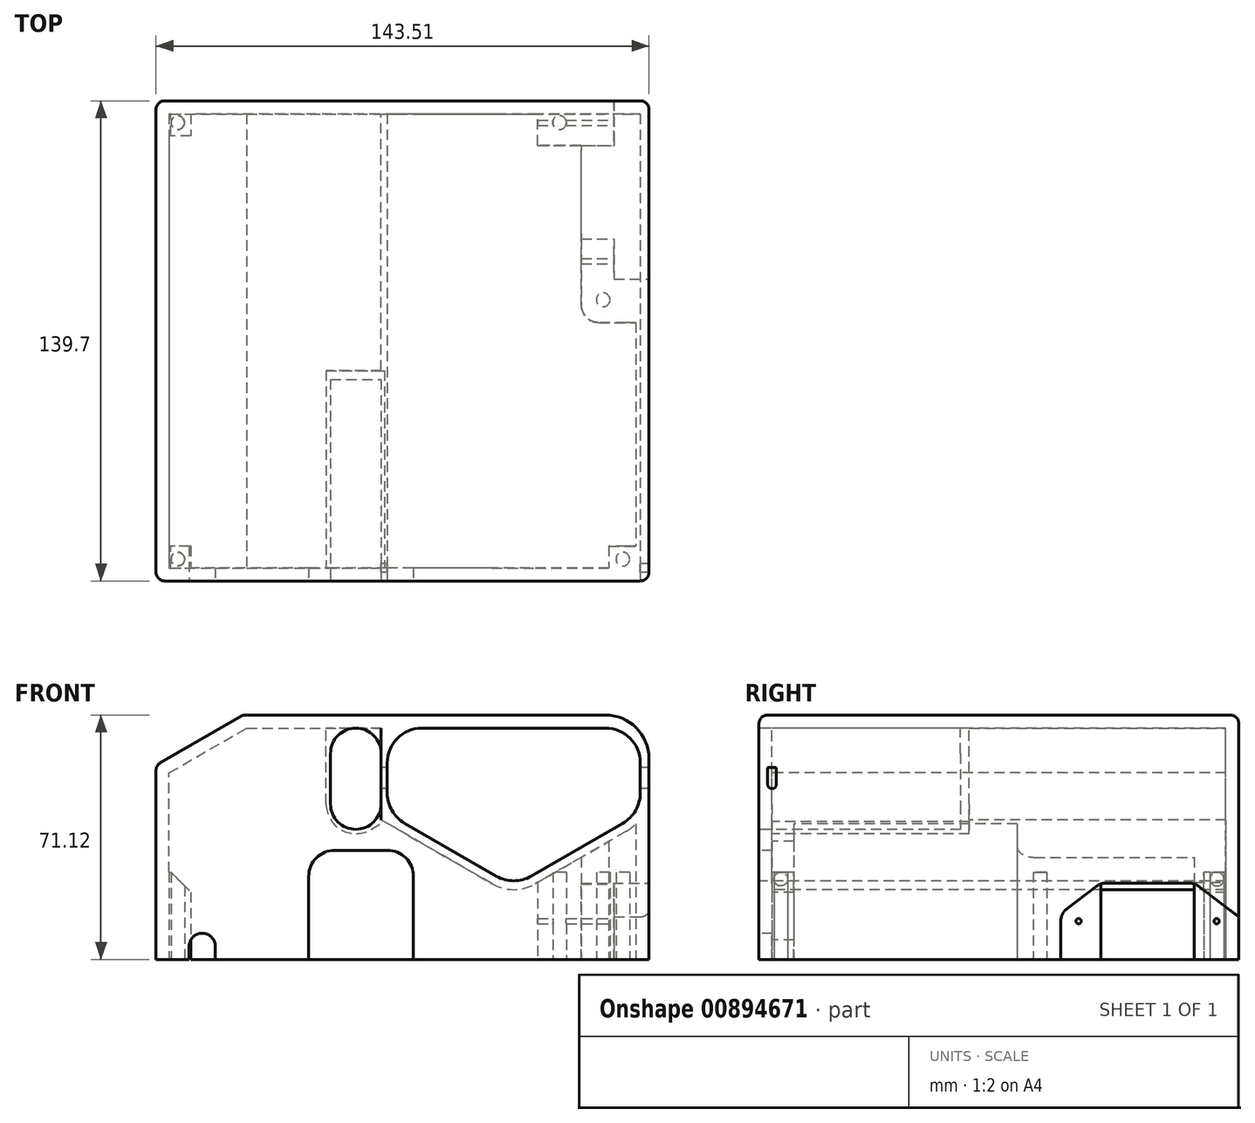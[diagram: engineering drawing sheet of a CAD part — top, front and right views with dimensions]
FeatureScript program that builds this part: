
annotation { "Feature Type Name" : "Feature", "Feature Type Description" : "" }
export const myFeature = defineFeature(function(context is Context, id is Id, definition is map)
    precondition{}
    {
        {
            var Q0;
            Q0=qCreatedBy(makeId("Top.planeOp"),FACE);
            var sketch = newSketch(context, id + "F0", { "sketchPlane" : qUnion([Q0])});
            skCircle(sketch, "E0", {"center": v(0, 127) * mm, "radius": 2 * mm});
            skCircle(sketch, "E1", {"center": v(0, 0) * mm, "radius": 2 * mm});
            skCircle(sketch, "E2", {"center": v(129.54, 0) * mm, "radius": 2 * mm});
            skCircle(sketch, "E3", {"center": v(123.83, 75.44) * mm, "radius": 2 * mm});
            skCircle(sketch, "E4", {"center": v(111.13, 127) * mm, "radius": 2 * mm});
            skSolve(sketch);
        }
        {
            var Q0;
            Q0=qCreatedBy(makeId("Front.planeOp"),FACE);
            var sketch = newSketch(context, id + "F1", { "sketchPlane" : qUnion([Q0])});
            skLineSegment(sketch, "E5", {"start": v(-6.35, 0) * mm, "end": v(-6.35, 56.46) * mm});
            skLineSegment(sketch, "E6", {"start": v(-6.35, 56.46) * mm, "end": v(19.05, 71.12) * mm});
            skLineSegment(sketch, "E7", {"start": v(19.05, 71.12) * mm, "end": v(124.46, 71.12) * mm});
            skLineSegment(sketch, "E8", {"start": v(137.16, 58.42) * mm, "end": v(137.16, 0) * mm});
            skLineSegment(sketch, "E9", {"start": v(137.16, 0) * mm, "end": v(-6.35, 0) * mm});
            skArc(sketch, "E10.filletArc", {"start": v(137.16, 58.42) * mm, "mid": v(133.44, 67.4) * mm, "end": v(124.46, 71.12) * mm});
            skSolve(sketch);
        }
        {
            var Q0;
            Q0=makeQuery(id+"F1.imprint","IMPRINT",FACE,{"disambiguationData":[TD([[makeQuery(id+"F1.imprint","IMPRINT",EDGE,{"derivedFrom":sQuery(id+"F1.wireOp",EDGE,"E5")}),-1.0]])]});
            extrude(context, id + "F2", {"entities" : qUnion([Q0]), "oppositeDirection" : true, "depth" : 133.35 * mm, "offsetDistance" : 25.4 * mm, "hasSecondDirection" : true, "secondDirectionOppositeDirection" : false, "secondDirectionDepth" : 6.35 * mm});
        }
        {
            var Q0;
            Q0=makeQuery(id+"F2.opExtrude","SWEPT_FACE",FACE,{"disambiguationData":[OSD([sQuery(id+"F1.wireOp",EDGE,"E9")])]});
            shell(context, id + "F3", {"entities" : qUnion([Q0]), "thickness" : 3.8 * mm});
        }
        {
            var Q0;
            Q0=makeQuery(id+"F2.opExtrude","SWEPT_FACE",FACE,{"disambiguationData":[OSD([sQuery(id+"F1.wireOp",EDGE,"E9")])]});
            var sketch = newSketch(context, id + "F4", { "sketchPlane" : qUnion([Q0])});
            skLineSegment(sketch, "E11", {"start": v(104.78, -129.54) * mm, "end": v(104.78, -120.4) * mm});
            skLineSegment(sketch, "E12", {"start": v(104.78, -120.4) * mm, "end": v(117.48, -120.4) * mm});
            skLineSegment(sketch, "E13", {"start": v(117.48, -120.4) * mm, "end": v(117.48, -68.83) * mm});
            skLineSegment(sketch, "E14", {"start": v(117.48, -68.83) * mm, "end": v(133.35, -68.83) * mm});
            skLineSegment(sketch, "E15", {"start": v(133.35, -68.83) * mm, "end": v(133.35, -129.54) * mm});
            skLineSegment(sketch, "E16", {"start": v(133.35, -129.54) * mm, "end": v(104.78, -129.54) * mm});
            skSolve(sketch);
        }
        {
            var Q0;
            Q0=makeQuery(id+"F4.imprint","IMPRINT",FACE,{"disambiguationData":[TD([[makeQuery(id+"F4.imprint","IMPRINT",EDGE,{"derivedFrom":sQuery(id+"F4.wireOp",EDGE,"E11")}),-1.0]])]});
            extrude(context, id + "F5", {"entities" : qUnion([Q0]), "operationType" : NewBodyOperationType.ADD, "endBound" : BoundingType.UP_TO_NEXT, "oppositeDirection" : true, "depth" : 25.4 * mm, "offsetDistance" : 25.4 * mm});
        }
        {
            var Q0;
            Q0=makeQuery(id+"F2.opExtrude","SWEPT_FACE",FACE,{"disambiguationData":[OSD([sQuery(id+"F1.wireOp",EDGE,"E8")])]});
            var sketch = newSketch(context, id + "F6", { "sketchPlane" : qUnion([Q0])});
            skArc(sketch, "E17", {"start": v(83.35, 14.77) * mm, "mid": v(82.01, 13.16) * mm, "end": v(81.53, 11.13) * mm});
            skLineSegment(sketch, "E18", {"start": v(83.35, 14.77) * mm, "end": v(91.97, 21.3) * mm});
            skLineSegment(sketch, "E19", {"start": v(94.73, 22.22) * mm, "end": v(118.86, 22.22) * mm});
            skLineSegment(sketch, "E20", {"start": v(121.62, 21.3) * mm, "end": v(133.35, 12.41) * mm});
            skLineSegment(sketch, "E21", {"start": v(133.35, 12.41) * mm, "end": v(133.35, 0) * mm});
            skPoint(sketch, "E22.visualSharp", {"position": v(93.19, 22.22) * mm});
            skArc(sketch, "E22.filletArc", {"start": v(94.73, 22.22) * mm, "mid": v(93.27, 21.99) * mm, "end": v(91.97, 21.3) * mm});
            skPoint(sketch, "E23.visualSharp", {"position": v(120.4, 22.23) * mm});
            skArc(sketch, "E23.filletArc", {"start": v(121.62, 21.3) * mm, "mid": v(120.31, 21.99) * mm, "end": v(118.86, 22.22) * mm});
            skLineSegment(sketch, "E24", {"start": v(81.53, -2.54) * mm, "end": v(133.35, -2.54) * mm});
            skLineSegment(sketch, "E25", {"start": v(133.35, -2.54) * mm, "end": v(133.35, 0) * mm});
            skLineSegment(sketch, "E26", {"start": v(81.53, 11.13) * mm, "end": v(81.53, -2.54) * mm});
            skSolve(sketch);
        }
        {
            var Q0;
            {var subQ4=sQuery(id+"F6.wireOp",EDGE,"E17");Q0=makeQuery(id+"F6.imprint","IMPRINT",FACE,{"disambiguationData":[TD([[makeQuery(id+"F6.imprint","IMPRINT",EDGE,{"derivedFrom":subQ4}),1.0]])]});}
            extrude(context, id + "F7", {"entities" : qUnion([Q0]), "operationType" : NewBodyOperationType.REMOVE, "oppositeDirection" : true, "depth" : 10.16 * mm, "offsetDistance" : 25.4 * mm});
        }
        {
            var Q0;
            Q0=makeQuery(id+"F7.boolean.opBoolean","COPY",FACE,{"derivedFrom":makeQuery(id+"F7.opExtrude","CAP_FACE",FACE,{"disambiguationData":[OSD([sQuery(id+"F1.wireOp",EDGE,"E8"),sQuery(id+"F1.wireOp",EDGE,"E9"),sQuery(id+"F6.wireOp",EDGE,"kEtzdfqh-l9jc-MdX5-V50T-5vboHq0TSI4w"),sQuery(id+"F6.wireOp",EDGE,"E17"),sQuery(id+"F6.wireOp",EDGE,"E18"),sQuery(id+"F6.wireOp",EDGE,"E19"),sQuery(id+"F6.wireOp",EDGE,"E20"),sQuery(id+"F6.wireOp",EDGE,"E21"),sQuery(id+"F6.wireOp",EDGE,"E22.filletArc"),sQuery(id+"F6.wireOp",EDGE,"E23.filletArc"),sQuery(id+"F6.wireOp",EDGE,"10d31ba4-3e29-4994-a5b2-82bfb8ec1515.filletArc")])],"isStart":false})});
            var sketch = newSketch(context, id + "F8", { "sketchPlane" : qUnion([Q0])});
            skLineSegment(sketch, "E27", {"start": v(93.22, 22.23) * mm, "end": v(120.4, 22.23) * mm});
            skLineSegment(sketch, "E28", {"start": v(120.4, 22.23) * mm, "end": v(120.4, 0) * mm});
            skLineSegment(sketch, "E29", {"start": v(120.4, 0) * mm, "end": v(93.22, 0) * mm});
            skLineSegment(sketch, "E30", {"start": v(93.22, 0) * mm, "end": v(93.22, 22.23) * mm});
            skCircle(sketch, "E31", {"center": v(86.72, 11.13) * mm, "radius": 0.76 * mm});
            skCircle(sketch, "E32", {"center": v(126.9, 11.13) * mm, "radius": 0.76 * mm});
            skSolve(sketch);
        }
        {
            var Q0;
            {var subQ0=sQuery(id+"F8.wireOp",EDGE,"E27");var subQ1=makeQuery(id+"F7.boolean.opBoolean","COPY",EDGE,{"derivedFrom":makeQuery(id+"F7.opExtrude","CAP_EDGE",EDGE,{"disambiguationData":[OSD([sQuery(id+"F6.wireOp",EDGE,"E22.filletArc")])],"isStart":false})});var subQ2=makeQuery(id+"F8.imprint","INTERSECT",VERTEX,{"derivedFrom":[subQ1,subQ0]});Q0=makeQuery(id+"F8.imprint","IMPRINT",FACE,{"disambiguationData":[TD([[makeQuery(id+"F8.imprint","IMPRINT",EDGE,{"disambiguationData":[TD([[subQ2,-1.0]])],"derivedFrom":subQ0}),-1.0]])]});}
            var Q1;
            Q1=makeQuery(id+"F8.imprint","IMPRINT",FACE,{"disambiguationData":[TD([[makeQuery(id+"F8.imprint","IMPRINT",EDGE,{"derivedFrom":sQuery(id+"F8.wireOp",EDGE,"E32")}),1.0]])]});
            var Q2;
            Q2=makeQuery(id+"F8.imprint","IMPRINT",FACE,{"disambiguationData":[TD([[makeQuery(id+"F8.imprint","IMPRINT",EDGE,{"derivedFrom":sQuery(id+"F8.wireOp",EDGE,"E31")}),1.0]])]});
            extrude(context, id + "F9", {"entities" : qUnion([Q0, Q1, Q2]), "operationType" : NewBodyOperationType.REMOVE, "oppositeDirection" : true, "depth" : 25.4 * mm, "offsetDistance" : 25.4 * mm});
        }
        {
            var Q0;
            Q0=makeQuery(id+"F2.opExtrude","CAP_FACE",FACE,{"disambiguationData":[OSD([sQuery(id+"F1.wireOp",EDGE,"E5"),sQuery(id+"F1.wireOp",EDGE,"E6"),sQuery(id+"F1.wireOp",EDGE,"E7"),sQuery(id+"F1.wireOp",EDGE,"E8"),sQuery(id+"F1.wireOp",EDGE,"E9"),sQuery(id+"F1.wireOp",EDGE,"E10.filletArc")])],"isStart":true});
            var sketch = newSketch(context, id + "F10", { "sketchPlane" : qUnion([Q0])});
            skArc(sketch, "E33", {"start": v(134.62, 57.15) * mm, "mid": v(131.64, 64.33) * mm, "end": v(124.46, 67.31) * mm});
            skArc(sketch, "E34", {"start": v(71.12, 67.31) * mm, "mid": v(63.94, 64.33) * mm, "end": v(60.96, 57.15) * mm});
            skLineSegment(sketch, "E35", {"start": v(71.12, 67.31) * mm, "end": v(124.46, 67.31) * mm});
            skLineSegment(sketch, "E36", {"start": v(134.62, 57.15) * mm, "end": v(134.62, 48.42) * mm});
            skLineSegment(sketch, "E37", {"start": v(60.96, 57.15) * mm, "end": v(60.96, 48.42) * mm});
            skArc(sketch, "E38", {"start": v(60.96, 48.42) * mm, "mid": v(62.32, 43.34) * mm, "end": v(66.04, 39.62) * mm});
            skArc(sketch, "E39", {"start": v(129.54, 39.62) * mm, "mid": v(133.26, 43.34) * mm, "end": v(134.62, 48.42) * mm});
            skLineSegment(sketch, "E40", {"start": v(66.04, 39.62) * mm, "end": v(92.71, 24.22) * mm});
            skLineSegment(sketch, "E41", {"start": v(102.87, 24.22) * mm, "end": v(129.54, 39.62) * mm});
            skArc(sketch, "E42", {"start": v(92.71, 24.22) * mm, "mid": v(97.8, 22.86) * mm, "end": v(102.87, 24.22) * mm});
            skArc(sketch, "E43", {"start": v(59.18, 59.94) * mm, "mid": v(51.82, 67.31) * mm, "end": v(44.45, 59.94) * mm});
            skArc(sketch, "E44", {"start": v(44.45, 45.21) * mm, "mid": v(51.82, 37.85) * mm, "end": v(59.18, 45.21) * mm});
            skLineSegment(sketch, "E45", {"start": v(44.45, 59.94) * mm, "end": v(44.45, 45.21) * mm});
            skLineSegment(sketch, "E46", {"start": v(59.18, 59.94) * mm, "end": v(59.18, 45.21) * mm});
            skLineSegment(sketch, "E47", {"start": v(56.93, 37.85) * mm, "end": v(38.82, 37.85) * mm, "construction": true});
            skSolve(sketch);
        }
        {
            var Q0;
            Q0 = qSketchRegion(id + "F10", true);
            var Q1;
            {var subQ0=sQuery(id+"F1.wireOp",EDGE,"E10.filletArc");var subQ1=sQuery(id+"F1.wireOp",EDGE,"E9");var subQ2=sQuery(id+"F1.wireOp",EDGE,"E8");var subQ3=sQuery(id+"F1.wireOp",EDGE,"E7");var subQ4=sQuery(id+"F1.wireOp",EDGE,"E6");var subQ5=sQuery(id+"F1.wireOp",EDGE,"E5");Q1=makeQuery(id+"F3.opShell","OFFSET_FACE",FACE,{"disambiguationData":[OSD([subQ5,subQ4,subQ3,subQ2,subQ1,subQ0]),TDD([makeQuery(id+"F2.opExtrude","CAP_FACE",FACE,{"disambiguationData":[OSD([subQ5,subQ4,subQ3,subQ2,subQ1,subQ0])],"isStart":false})])]});}
            extrude(context, id + "F11", {"entities" : qUnion([Q0]), "operationType" : NewBodyOperationType.REMOVE, "endBound" : BoundingType.UP_TO_SURFACE, "oppositeDirection" : true, "depth" : 25.4 * mm, "endBoundEntityFace" : qUnion([Q1]), "offsetDistance" : 25.4 * mm});
        }
        {
            var Q0;
            Q0=makeQuery(id+"F2.opExtrude","CAP_FACE",FACE,{"disambiguationData":[OSD([sQuery(id+"F1.wireOp",EDGE,"E5"),sQuery(id+"F1.wireOp",EDGE,"E6"),sQuery(id+"F1.wireOp",EDGE,"E7"),sQuery(id+"F1.wireOp",EDGE,"E8"),sQuery(id+"F1.wireOp",EDGE,"E9"),sQuery(id+"F1.wireOp",EDGE,"E10.filletArc")])],"isStart":true});
            var sketch = newSketch(context, id + "F12", { "sketchPlane" : qUnion([Q0])});
            skArc(sketch, "E48", {"start": v(91.44, 22.02) * mm, "mid": v(97.8, 20.32) * mm, "end": v(104.14, 22.02) * mm});
            skLineSegment(sketch, "E49", {"start": v(91.44, 22.02) * mm, "end": v(59.18, 40.65) * mm});
            skLineSegment(sketch, "E50", {"start": v(104.14, 22.02) * mm, "end": v(130.48, 37.23) * mm});
            skLineSegment(sketch, "E51", {"start": v(59.18, 71.12) * mm, "end": v(124.46, 71.12) * mm});
            skArc(sketch, "E52", {"start": v(137.16, 58.42) * mm, "mid": v(133.44, 67.4) * mm, "end": v(124.46, 71.12) * mm});
            skLineSegment(sketch, "E53", {"start": v(137.16, 58.42) * mm, "end": v(137.16, 48.8) * mm});
            skArc(sketch, "E54", {"start": v(130.48, 37.23) * mm, "mid": v(135.37, 42.12) * mm, "end": v(137.16, 48.8) * mm});
            skLineSegment(sketch, "E55", {"start": v(92.71, 24.22) * mm, "end": v(66.04, 39.62) * mm});
            skLineSegment(sketch, "E56", {"start": v(71.12, 67.31) * mm, "end": v(124.46, 67.31) * mm});
            skLineSegment(sketch, "E57", {"start": v(134.62, 57.15) * mm, "end": v(134.62, 48.42) * mm});
            skLineSegment(sketch, "E58", {"start": v(129.54, 39.62) * mm, "end": v(102.87, 24.22) * mm});
            skArc(sketch, "E59", {"start": v(92.71, 24.22) * mm, "mid": v(97.8, 22.86) * mm, "end": v(102.87, 24.22) * mm});
            skArc(sketch, "E60", {"start": v(129.54, 39.62) * mm, "mid": v(133.26, 43.34) * mm, "end": v(134.62, 48.42) * mm});
            skArc(sketch, "E61", {"start": v(134.62, 57.15) * mm, "mid": v(131.64, 64.33) * mm, "end": v(124.46, 67.31) * mm});
            skArc(sketch, "E62", {"start": v(71.12, 67.31) * mm, "mid": v(63.94, 64.33) * mm, "end": v(60.96, 57.15) * mm});
            skLineSegment(sketch, "E63", {"start": v(60.96, 57.15) * mm, "end": v(60.96, 48.42) * mm});
            skArc(sketch, "E64", {"start": v(60.96, 48.42) * mm, "mid": v(62.32, 43.34) * mm, "end": v(66.04, 39.62) * mm});
            skLineSegment(sketch, "E65", {"start": v(59.18, 71.12) * mm, "end": v(59.18, 40.65) * mm});
            skSolve(sketch);
        }
        {
            var Q0;
            Q0=makeQuery(id+"F12.imprint","IMPRINT",FACE,{"disambiguationData":[TD([[makeQuery(id+"F12.imprint","IMPRINT",EDGE,{"derivedFrom":sQuery(id+"F12.wireOp",EDGE,"E48")}),1.0]])]});
            var Q1;
            {var subQ0=sQuery(id+"F1.wireOp",EDGE,"E10.filletArc");var subQ1=sQuery(id+"F1.wireOp",EDGE,"E9");var subQ2=sQuery(id+"F1.wireOp",EDGE,"E8");var subQ3=sQuery(id+"F1.wireOp",EDGE,"E7");var subQ4=sQuery(id+"F1.wireOp",EDGE,"E6");var subQ5=sQuery(id+"F1.wireOp",EDGE,"E5");Q1=makeQuery(id+"F11.boolean.opBoolean","MERGE",FACE,{"derivedFrom":[makeQuery(id+"F3.opShell","OFFSET_FACE",FACE,{"disambiguationData":[OSD([subQ5,subQ4,subQ3,subQ2,subQ1,subQ0]),TDD([makeQuery(id+"F2.opExtrude","CAP_FACE",FACE,{"disambiguationData":[OSD([subQ5,subQ4,subQ3,subQ2,subQ1,subQ0])],"isStart":false})])]})],"fromTools":[makeQuery(id+"F11.opExtrude","CAP_FACE",FACE,{"disambiguationData":[OSD([sQuery(id+"F10.wireOp",EDGE,"E33"),sQuery(id+"F10.wireOp",EDGE,"E34"),sQuery(id+"F10.wireOp",EDGE,"E35"),sQuery(id+"F10.wireOp",EDGE,"E36"),sQuery(id+"F10.wireOp",EDGE,"E37"),sQuery(id+"F10.wireOp",EDGE,"E38"),sQuery(id+"F10.wireOp",EDGE,"E39"),sQuery(id+"F10.wireOp",EDGE,"E40"),sQuery(id+"F10.wireOp",EDGE,"E41"),sQuery(id+"F10.wireOp",EDGE,"E42")])],"isStart":false})]});}
            extrude(context, id + "F13", {"entities" : qUnion([Q0]), "operationType" : NewBodyOperationType.ADD, "endBound" : BoundingType.UP_TO_SURFACE, "oppositeDirection" : true, "depth" : 25.4 * mm, "endBoundEntityFace" : qUnion([Q1]), "offsetDistance" : 25.4 * mm});
        }
        {
            var Q0;
            Q0=makeQuery(id+"F2.opExtrude","CAP_FACE",FACE,{"disambiguationData":[OSD([sQuery(id+"F1.wireOp",EDGE,"E5"),sQuery(id+"F1.wireOp",EDGE,"E6"),sQuery(id+"F1.wireOp",EDGE,"E7"),sQuery(id+"F1.wireOp",EDGE,"E8"),sQuery(id+"F1.wireOp",EDGE,"E9"),sQuery(id+"F1.wireOp",EDGE,"E10.filletArc")])],"isStart":true});
            var sketch = newSketch(context, id + "F14", { "sketchPlane" : qUnion([Q0])});
            skLineSegment(sketch, "E66", {"start": v(68.58, 24.13) * mm, "end": v(68.58, -2.54) * mm});
            skLineSegment(sketch, "E67", {"start": v(68.58, -2.54) * mm, "end": v(38.1, -2.54) * mm});
            skLineSegment(sketch, "E68", {"start": v(38.1, -2.54) * mm, "end": v(38.1, 24.13) * mm});
            skArc(sketch, "E69", {"start": v(45.72, 31.75) * mm, "mid": v(40.33, 29.52) * mm, "end": v(38.1, 24.13) * mm});
            skArc(sketch, "E70", {"start": v(68.58, 24.13) * mm, "mid": v(66.35, 29.52) * mm, "end": v(60.96, 31.75) * mm});
            skLineSegment(sketch, "E71", {"start": v(60.96, 31.75) * mm, "end": v(45.72, 31.75) * mm});
            skLineSegment(sketch, "E72", {"start": v(10.92, -1.27) * mm, "end": v(10.92, 3.8) * mm});
            skLineSegment(sketch, "E73", {"start": v(10.92, -1.27) * mm, "end": v(3.3, -1.27) * mm});
            skLineSegment(sketch, "E74", {"start": v(3.3, -1.27) * mm, "end": v(3.3, 3.8) * mm});
            skArc(sketch, "E75", {"start": v(10.92, 3.8) * mm, "mid": v(7.11, 7.62) * mm, "end": v(3.3, 3.8) * mm});
            skSolve(sketch);
        }
        {
            var Q0;
            {var subQ0=sQuery(id+"F14.wireOp",EDGE,"E75");Q0=makeQuery(id+"F14.imprint","IMPRINT",FACE,{"disambiguationData":[TD([[makeQuery(id+"F14.imprint","IMPRINT",EDGE,{"derivedFrom":subQ0}),1.0]])]});}
            var Q1;
            {var subQ1=sQuery(id+"F14.wireOp",EDGE,"E69");Q1=makeQuery(id+"F14.imprint","IMPRINT",FACE,{"disambiguationData":[TD([[makeQuery(id+"F14.imprint","IMPRINT",EDGE,{"derivedFrom":subQ1}),1.0]])]});}
            extrude(context, id + "F15", {"entities" : qUnion([Q0, Q1]), "operationType" : NewBodyOperationType.REMOVE, "oppositeDirection" : true, "depth" : 25.4 * mm, "offsetDistance" : 25.4 * mm});
        }
        {
            var Q0;
            Q0=makeQuery(id+"F2.opExtrude","CAP_FACE",FACE,{"disambiguationData":[OSD([sQuery(id+"F1.wireOp",EDGE,"E5"),sQuery(id+"F1.wireOp",EDGE,"E6"),sQuery(id+"F1.wireOp",EDGE,"E7"),sQuery(id+"F1.wireOp",EDGE,"E8"),sQuery(id+"F1.wireOp",EDGE,"E9"),sQuery(id+"F1.wireOp",EDGE,"E10.filletArc")])],"isStart":true});
            var sketch = newSketch(context, id + "F16", { "sketchPlane" : qUnion([Q0])});
            skArc(sketch, "E76", {"start": v(59.18, 59.94) * mm, "mid": v(51.82, 67.31) * mm, "end": v(44.45, 59.94) * mm});
            skArc(sketch, "E77", {"start": v(44.45, 45.21) * mm, "mid": v(51.82, 37.85) * mm, "end": v(59.18, 45.21) * mm});
            skLineSegment(sketch, "E78", {"start": v(44.45, 59.94) * mm, "end": v(44.45, 45.21) * mm});
            skLineSegment(sketch, "E79", {"start": v(59.18, 59.94) * mm, "end": v(59.18, 45.21) * mm});
            skArc(sketch, "E80", {"start": v(43.18, 45.21) * mm, "mid": v(47.53, 37.71) * mm, "end": v(56.2, 37.77) * mm});
            skLineSegment(sketch, "E81", {"start": v(43.18, 45.21) * mm, "end": v(43.18, 69.85) * mm});
            skLineSegment(sketch, "E82", {"start": v(43.18, 69.85) * mm, "end": v(60.9, 69.85) * mm});
            skLineSegment(sketch, "E83", {"start": v(60.96, 48.42) * mm, "end": v(60.96, 48.42) * mm});
            skLineSegment(sketch, "E84", {"start": v(56.2, 37.77) * mm, "end": v(60.14, 40.1) * mm});
            skLineSegment(sketch, "E85", {"start": v(60.9, 69.85) * mm, "end": v(60.9, 42.16) * mm});
            skLineSegment(sketch, "E86", {"start": v(60.9, 42.16) * mm, "end": v(60.14, 40.1) * mm});
            skSolve(sketch);
        }
        {
            var Q0;
            Q0=makeQuery(id+"F16.imprint","IMPRINT",FACE,{"disambiguationData":[TD([[makeQuery(id+"F16.imprint","IMPRINT",EDGE,{"derivedFrom":sQuery(id+"F16.wireOp",EDGE,"E76")}),-1.0]])]});
            extrude(context, id + "F17", {"entities" : qUnion([Q0]), "operationType" : NewBodyOperationType.ADD, "oppositeDirection" : true, "depth" : 73.66 * mm - 12.45 * mm, "offsetDistance" : 25.4 * mm});
        }
        {
            var Q0;
            {var subQ0=sQuery(id+"F16.wireOp",EDGE,"E78");var subQ1=sQuery(id+"F16.wireOp",EDGE,"E77");var subQ2=sQuery(id+"F16.wireOp",EDGE,"E81");var subQ3=sQuery(id+"F16.wireOp",EDGE,"E80");var subQ4=sQuery(id+"F16.wireOp",EDGE,"E76");var subQ5=makeQuery(id+"F17.opExtrude","CAP_FACE",FACE,{"disambiguationData":[OSD([subQ4,subQ1,subQ0,sQuery(id+"F16.wireOp",EDGE,"E79"),subQ3,subQ2,sQuery(id+"F16.wireOp",EDGE,"E82"),sQuery(id+"F16.wireOp",EDGE,"U3WXS13F-Hr26-8joM-5xUV-uJcK7qQu7TBT")])],"isStart":false});Q0=makeQuery(id+"F17.boolean.opBoolean","SPLIT",FACE,{"disambiguationData":[TD([makeQuery(id+"F3.opShell","OFFSET_FACE",FACE,{"disambiguationData":[OSD([sQuery(id+"F1.wireOp",EDGE,"E7")])]}),makeQuery(id+"F11.boolean.opBoolean","COPY",FACE,{"derivedFrom":makeQuery(id+"F11.opExtrude","SWEPT_FACE",FACE,{"disambiguationData":[OSD([sQuery(id+"F10.wireOp",EDGE,"E43")])]})}),makeQuery(id+"F11.boolean.opBoolean","COPY",FACE,{"derivedFrom":makeQuery(id+"F11.opExtrude","SWEPT_FACE",FACE,{"disambiguationData":[OSD([sQuery(id+"F10.wireOp",EDGE,"E44")])]})}),makeQuery(id+"F11.boolean.opBoolean","COPY",FACE,{"derivedFrom":makeQuery(id+"F11.opExtrude","SWEPT_FACE",FACE,{"disambiguationData":[OSD([sQuery(id+"F10.wireOp",EDGE,"E45")])]})}),makeQuery(id+"F11.boolean.opBoolean","COPY",FACE,{"derivedFrom":makeQuery(id+"F11.opExtrude","SWEPT_FACE",FACE,{"disambiguationData":[OSD([sQuery(id+"F10.wireOp",EDGE,"E46")])]})}),makeQuery(id+"F13.opExtrude","SWEPT_FACE",FACE,{"disambiguationData":[OSD([sQuery(id+"F12.wireOp",EDGE,"E65")])]}),makeQuery(id+"F17.opExtrude","SWEPT_FACE",FACE,{"disambiguationData":[OSD([subQ4])]}),subQ5,makeQuery(id+"F17.opExtrude","SWEPT_FACE",FACE,{"disambiguationData":[OSD([subQ1])]}),makeQuery(id+"F17.opExtrude","SWEPT_FACE",FACE,{"disambiguationData":[OSD([subQ0])]}),makeQuery(id+"F17.opExtrude","SWEPT_FACE",FACE,{"disambiguationData":[OSD([subQ3])]}),makeQuery(id+"F17.opExtrude","SWEPT_FACE",FACE,{"disambiguationData":[OSD([subQ2])]})])],"derivedFrom":subQ5});}
            var sketch = newSketch(context, id + "F18", { "sketchPlane" : qUnion([Q0])});
            skLineSegment(sketch, "E87", {"start": v(-43.18, 45.21) * mm, "end": v(-43.18, 67.31) * mm});
            skLineSegment(sketch, "E88", {"start": v(-43.18, 67.31) * mm, "end": v(-59.18, 67.31) * mm});
            skLineSegment(sketch, "E89", {"start": v(-59.18, 67.31) * mm, "end": v(-59.18, 40.65) * mm});
            skArc(sketch, "E90", {"start": v(-56.2, 37.77) * mm, "mid": v(-47.53, 37.71) * mm, "end": v(-43.18, 45.21) * mm});
            skLineSegment(sketch, "E91", {"start": v(-56.2, 37.77) * mm, "end": v(-60.14, 40.1) * mm});
            skLineSegment(sketch, "E92", {"start": v(-60.14, 40.1) * mm, "end": v(-59.18, 40.65) * mm});
            skSolve(sketch);
        }
        {
            var Q0;
            Q0 = qSketchRegion(id + "F18", true);
            extrude(context, id + "F19", {"entities" : qUnion([Q0]), "operationType" : NewBodyOperationType.ADD, "oppositeDirection" : true, "depth" : 2.54 * mm, "offsetDistance" : 25.4 * mm});
        }
        {
            var Q0;
            {var subQ1=sQuery(id+"F1.wireOp",EDGE,"E9");var subQ5=sQuery(id+"F1.wireOp",EDGE,"E5");var subQ8=sQuery(id+"F4.wireOp",EDGE,"E11");var subQ9=sQuery(id+"F4.wireOp",EDGE,"E12");Q0=makeQuery(id+"F15.boolean.opBoolean","SPLIT",FACE,{"disambiguationData":[TD([makeQuery(id+"F2.opExtrude","SWEPT_FACE",FACE,{"disambiguationData":[OSD([subQ5])]})])],"derivedFrom":makeQuery(id+"F5.boolean.opBoolean","MERGE",FACE,{"derivedFrom":[makeQuery(id+"F2.opExtrude","SWEPT_FACE",FACE,{"disambiguationData":[OSD([subQ1])]}),makeQuery(id+"F5.opExtrude","CAP_FACE",FACE,{"disambiguationData":[OSD([subQ8,subQ9,sQuery(id+"F4.wireOp",EDGE,"E13"),sQuery(id+"F4.wireOp",EDGE,"E14"),sQuery(id+"F4.wireOp",EDGE,"E15"),sQuery(id+"F4.wireOp",EDGE,"E16")])],"isStart":true})]})});}
            var sketch = newSketch(context, id + "F20", { "sketchPlane" : qUnion([Q0])});
            skLineSegment(sketch, "E93", {"start": v(3.81, 2.54) * mm, "end": v(3.81, -3.8) * mm});
            skLineSegment(sketch, "E94", {"start": v(3.81, -3.8) * mm, "end": v(-2.54, -3.81) * mm});
            skLineSegment(sketch, "E95", {"start": v(-2.54, -3.81) * mm, "end": v(-2.54, 2.54) * mm});
            skLineSegment(sketch, "E96", {"start": v(-2.54, 2.54) * mm, "end": v(3.81, 2.54) * mm});
            skLineSegment(sketch, "E97", {"start": v(3.81, -129.54) * mm, "end": v(3.81, -123.2) * mm});
            skLineSegment(sketch, "E98", {"start": v(3.81, -123.2) * mm, "end": v(-2.54, -123.2) * mm});
            skLineSegment(sketch, "E99", {"start": v(-2.54, -123.2) * mm, "end": v(-2.54, -129.54) * mm});
            skLineSegment(sketch, "E100", {"start": v(-2.54, -129.54) * mm, "end": v(3.81, -129.54) * mm});
            skSolve(sketch);
        }
        {
            var Q0;
            {var subQ1=sQuery(id+"F1.wireOp",EDGE,"E9");var subQ2=sQuery(id+"F1.wireOp",EDGE,"E8");var subQ7=sQuery(id+"F4.wireOp",EDGE,"E14");var subQ8=sQuery(id+"F4.wireOp",EDGE,"E13");Q0=makeQuery(id+"F15.boolean.opBoolean","SPLIT",FACE,{"disambiguationData":[TD([makeQuery(id+"F2.opExtrude","SWEPT_FACE",FACE,{"disambiguationData":[OSD([subQ2])]})])],"derivedFrom":makeQuery(id+"F5.boolean.opBoolean","MERGE",FACE,{"derivedFrom":[makeQuery(id+"F2.opExtrude","SWEPT_FACE",FACE,{"disambiguationData":[OSD([subQ1])]}),makeQuery(id+"F5.opExtrude","CAP_FACE",FACE,{"disambiguationData":[OSD([sQuery(id+"F4.wireOp",EDGE,"E11"),sQuery(id+"F4.wireOp",EDGE,"E12"),subQ8,subQ7,sQuery(id+"F4.wireOp",EDGE,"E15"),sQuery(id+"F4.wireOp",EDGE,"E16")])],"isStart":true})]})});}
            var sketch = newSketch(context, id + "F21", { "sketchPlane" : qUnion([Q0])});
            skLineSegment(sketch, "E101", {"start": v(133.35, 2.54) * mm, "end": v(125.48, 2.54) * mm});
            skLineSegment(sketch, "E102", {"start": v(125.48, 2.54) * mm, "end": v(125.48, -3.8) * mm});
            skLineSegment(sketch, "E103", {"start": v(125.48, -3.8) * mm, "end": v(133.35, -3.8) * mm});
            skLineSegment(sketch, "E104", {"start": v(133.35, -3.8) * mm, "end": v(133.35, 2.54) * mm});
            skSolve(sketch);
        }
        {
            var Q0;
            Q0 = qSketchRegion(id + "F21", true);
            extrude(context, id + "F22", {"entities" : qUnion([Q0]), "operationType" : NewBodyOperationType.ADD, "endBound" : BoundingType.UP_TO_NEXT, "oppositeDirection" : true, "depth" : 25.4 * mm, "offsetDistance" : 25.4 * mm});
        }
        {
            var Q0;
            Q0 = qSketchRegion(id + "F20", true);
            extrude(context, id + "F23", {"entities" : qUnion([Q0]), "operationType" : NewBodyOperationType.ADD, "oppositeDirection" : true, "depth" : 25.4 * mm, "offsetDistance" : 25.4 * mm});
        }
        {
            var Q0;
            Q0=makeQuery(id+"F23.opExtrude","CAP_EDGE",EDGE,{"disambiguationData":[OSD([sQuery(id+"F20.wireOp",EDGE,"E93")])],"isStart":false});
            var Q1;
            Q1=makeQuery(id+"F23.opExtrude","CAP_EDGE",EDGE,{"disambiguationData":[OSD([sQuery(id+"F20.wireOp",EDGE,"E97")])],"isStart":false});
            chamfer(context, id + "F24", {"entities" : qUnion([Q0, Q1]), "width" : 5.84 * mm, "tangentPropagation" : true});
        }
        {
            var Q0;
            Q0=makeQuery(id+"F13.boolean.opBoolean","MERGE",FACE,{"derivedFrom":[makeQuery(id+"F11.boolean.opBoolean","COPY",FACE,{"derivedFrom":makeQuery(id+"F11.opExtrude","SWEPT_FACE",FACE,{"disambiguationData":[OSD([sQuery(id+"F10.wireOp",EDGE,"E37")])]})}),makeQuery(id+"F13.opExtrude","SWEPT_FACE",FACE,{"disambiguationData":[OSD([sQuery(id+"F12.wireOp",EDGE,"E63")])]})]});
            var sketch = newSketch(context, id + "F25", { "sketchPlane" : qUnion([Q0])});
            skArc(sketch, "E105", {"start": v(-3.81, 50.96) * mm, "mid": v(-2.54, 49.69) * mm, "end": v(-1.27, 50.96) * mm});
            skLineSegment(sketch, "E106", {"start": v(-3.8, 50.96) * mm, "end": v(-3.81, 55.88) * mm});
            skLineSegment(sketch, "E107", {"start": v(-3.81, 55.88) * mm, "end": v(-1.27, 55.88) * mm});
            skLineSegment(sketch, "E108", {"start": v(-1.27, 55.88) * mm, "end": v(-1.27, 50.96) * mm});
            skSolve(sketch);
        }
        {
            var Q0;
            Q0 = qSketchRegion(id + "F25", true);
            extrude(context, id + "F26", {"entities" : qUnion([Q0]), "operationType" : NewBodyOperationType.REMOVE, "depth" : 76.2 * mm, "hasOffset" : true, "offsetDistance" : 1.27 * mm, "hasSecondDirection" : true, "secondDirectionOppositeDirection" : true, "secondDirectionDepth" : 2.54 * mm});
        }
        {
            var Q0;
            Q0 = qSketchRegion(id + "F0", true);
            extrude(context, id + "F27", {"entities" : qUnion([Q0]), "operationType" : NewBodyOperationType.REMOVE, "depth" : 25.4 * mm, "offsetDistance" : 25.4 * mm});
        }
        {
            var Q0;
            Q0=makeQuery(id+"F2.opExtrude","CAP_EDGE",EDGE,{"disambiguationData":[OSD([sQuery(id+"F1.wireOp",EDGE,"E8")])],"isStart":true});
            var Q1;
            Q1=makeQuery(id+"F2.opExtrude","CAP_EDGE",EDGE,{"disambiguationData":[OSD([sQuery(id+"F1.wireOp",EDGE,"E6")])],"isStart":true});
            var Q2;
            Q2=makeQuery(id+"F2.opExtrude","CAP_EDGE",EDGE,{"disambiguationData":[OSD([sQuery(id+"F1.wireOp",EDGE,"E5")])],"isStart":true});
            var Q3;
            Q3=makeQuery(id+"F2.opExtrude","SWEPT_EDGE",EDGE,{"disambiguationData":[OSD([sQuery(id+"F1.wireOp",EDGE,"E5"),sQuery(id+"F1.wireOp",EDGE,"E6")])]});
            var Q4;
            Q4=makeQuery(id+"F2.opExtrude","SWEPT_EDGE",EDGE,{"disambiguationData":[OSD([sQuery(id+"F1.wireOp",EDGE,"E6"),sQuery(id+"F1.wireOp",EDGE,"E7")])]});
            var Q5;
            Q5=makeQuery(id+"F2.opExtrude","CAP_EDGE",EDGE,{"disambiguationData":[OSD([sQuery(id+"F1.wireOp",EDGE,"E5")])],"isStart":false});
            var Q6;
            Q6=makeQuery(id+"F2.opExtrude","CAP_EDGE",EDGE,{"disambiguationData":[OSD([sQuery(id+"F1.wireOp",EDGE,"E6")])],"isStart":false});
            var Q7;
            Q7=makeQuery(id+"F2.opExtrude","CAP_EDGE",EDGE,{"disambiguationData":[OSD([sQuery(id+"F1.wireOp",EDGE,"E7")])],"isStart":false});
            fillet(context, id + "F28", {"entities" : qUnion([Q0, Q1, Q2, Q3, Q4, Q5, Q6, Q7]), "radius" : 2.54 * mm, "tangentPropagation" : true, "allowEdgeOverflow" : false});
        }
        {
            var Q0;
            Q0=makeQuery(id+"F23.opExtrude","SWEPT_FACE",FACE,{"disambiguationData":[OSD([sQuery(id+"F20.wireOp",EDGE,"E96")])]});
            extrude(context, id + "F29", {"entities" : qUnion([Q0]), "operationType" : NewBodyOperationType.REMOVE, "oppositeDirection" : true, "depth" : 25.4 * mm, "offsetDistance" : 25.4 * mm});
        }
        {
            var Q0;
            Q0=makeQuery(id+"F23.opExtrude","SWEPT_EDGE",EDGE,{"disambiguationData":[OSD([sQuery(id+"F1.wireOp",EDGE,"E5"),sQuery(id+"F1.wireOp",EDGE,"E9"),sQuery(id+"F20.wireOp",EDGE,"E94"),sQuery(id+"F20.wireOp",EDGE,"E95")])]});
            var Q1;
            {var subQ0=sQuery(id+"F1.wireOp",EDGE,"E10.filletArc");var subQ1=sQuery(id+"F1.wireOp",EDGE,"E9");var subQ2=sQuery(id+"F1.wireOp",EDGE,"E8");var subQ3=sQuery(id+"F1.wireOp",EDGE,"E7");var subQ4=sQuery(id+"F1.wireOp",EDGE,"E6");var subQ5=sQuery(id+"F1.wireOp",EDGE,"E5");var subQ6=sQuery(id+"F20.wireOp",EDGE,"E93");Q1=makeQuery(id+"F23.boolean.opBoolean","SPLIT",EDGE,{"disambiguationData":[topologyDisambiguationEdgeConnected([makeQuery(id+"F3.opShell","OFFSET_FACE",FACE,{"disambiguationData":[OSD([subQ5,subQ4,subQ3,subQ2,subQ1,subQ0]),TDD([makeQuery(id+"F2.opExtrude","CAP_FACE",FACE,{"disambiguationData":[OSD([subQ5,subQ4,subQ3,subQ2,subQ1,subQ0])],"isStart":true})])]})])],"derivedFrom":makeQuery(id+"F23.opExtrude","SWEPT_EDGE",EDGE,{"disambiguationData":[OSD([subQ6,sQuery(id+"F20.wireOp",EDGE,"E96")])]})});}
            var Q2;
            Q2=makeQuery(id+"F23.opExtrude","SWEPT_EDGE",EDGE,{"disambiguationData":[OSD([sQuery(id+"F1.wireOp",EDGE,"E5"),sQuery(id+"F1.wireOp",EDGE,"E9"),sQuery(id+"F20.wireOp",EDGE,"E98"),sQuery(id+"F20.wireOp",EDGE,"E99")])]});
            var Q3;
            Q3=makeQuery(id+"F23.opExtrude","SWEPT_EDGE",EDGE,{"disambiguationData":[OSD([sQuery(id+"F1.wireOp",EDGE,"E9"),sQuery(id+"F20.wireOp",EDGE,"E97"),sQuery(id+"F20.wireOp",EDGE,"E100")])]});
            var Q4;
            Q4=makeQuery(id+"F22.opExtrude","SWEPT_EDGE",EDGE,{"disambiguationData":[OSD([sQuery(id+"F1.wireOp",EDGE,"E9"),sQuery(id+"F21.wireOp",EDGE,"E101"),sQuery(id+"F21.wireOp",EDGE,"E102")])]});
            var Q5;
            Q5=makeQuery(id+"F22.opExtrude","SWEPT_EDGE",EDGE,{"disambiguationData":[OSD([sQuery(id+"F1.wireOp",EDGE,"E8"),sQuery(id+"F1.wireOp",EDGE,"E9"),sQuery(id+"F21.wireOp",EDGE,"E103"),sQuery(id+"F21.wireOp",EDGE,"E104")])]});
            var Q6;
            Q6=makeQuery(id+"F5.opExtrude","SWEPT_EDGE",EDGE,{"disambiguationData":[OSD([sQuery(id+"F1.wireOp",EDGE,"E8"),sQuery(id+"F1.wireOp",EDGE,"E9"),sQuery(id+"F4.wireOp",EDGE,"E14"),sQuery(id+"F4.wireOp",EDGE,"E15")])]});
            var Q7;
            Q7=makeQuery(id+"F5.opExtrude","SWEPT_EDGE",EDGE,{"disambiguationData":[OSD([sQuery(id+"F4.wireOp",EDGE,"E13"),sQuery(id+"F4.wireOp",EDGE,"E14")])]});
            var Q8;
            Q8=makeQuery(id+"F5.opExtrude","SWEPT_EDGE",EDGE,{"disambiguationData":[OSD([sQuery(id+"F1.wireOp",EDGE,"E9"),sQuery(id+"F4.wireOp",EDGE,"E11"),sQuery(id+"F4.wireOp",EDGE,"E16")])]});
            fillet(context, id + "F30", {"entities" : qUnion([Q0, Q1, Q2, Q3, Q4, Q5, Q6, Q7, Q8]), "radius" : 5.08 * mm, "tangentPropagation" : true, "allowEdgeOverflow" : false});
        }
    });
